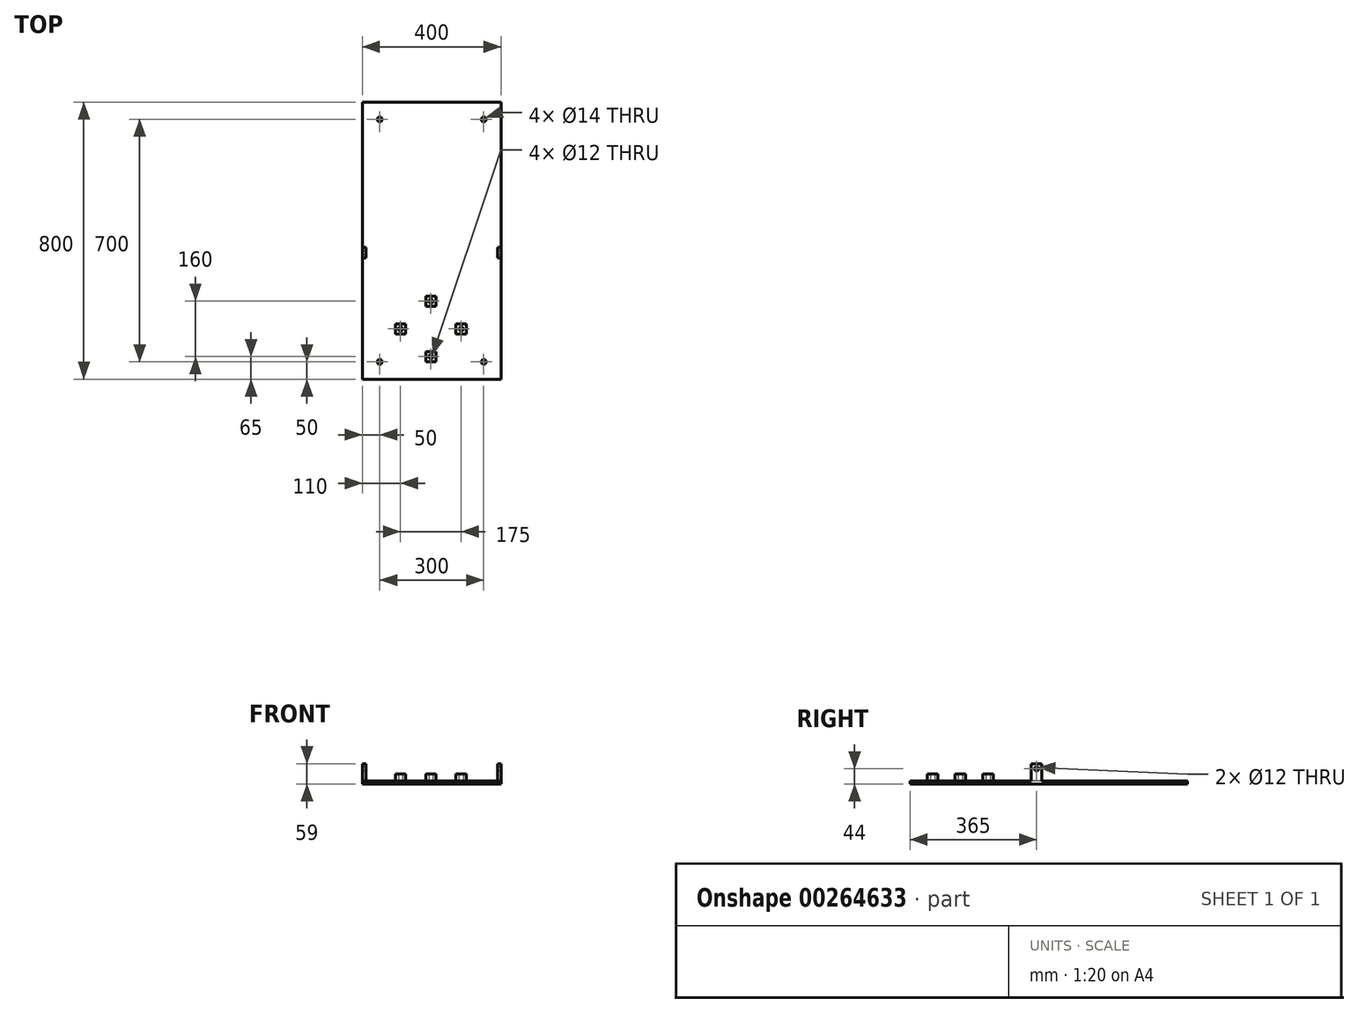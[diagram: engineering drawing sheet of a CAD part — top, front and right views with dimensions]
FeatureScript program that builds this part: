
annotation { "Feature Type Name" : "Feature", "Feature Type Description" : "" }
export const myFeature = defineFeature(function(context is Context, id is Id, definition is map)
    precondition{}
    {
        {
            var Q0;
            Q0=qCreatedBy(makeId("Top.planeOp"),FACE);
            var sketch = newSketch(context, id + "F0", { "sketchPlane" : qUnion([Q0])});
            skLineSegment(sketch, "E0.bottom", {"start": v(0, 0) * mm, "end": v(400, 0) * mm});
            skLineSegment(sketch, "E0.top", {"start": v(0, 800) * mm, "end": v(400, 800) * mm});
            skLineSegment(sketch, "E0.left", {"start": v(0, 0) * mm, "end": v(0, 800) * mm});
            skLineSegment(sketch, "E0.right", {"start": v(400, 0) * mm, "end": v(400, 800) * mm});
            skLineSegment(sketch, "E1.0", {"start": v(50, 50) * mm, "end": v(50, 750) * mm, "construction": true});
            skLineSegment(sketch, "E1.1", {"start": v(50, 50) * mm, "end": v(350, 50) * mm, "construction": true});
            skLineSegment(sketch, "E1.2", {"start": v(350, 50) * mm, "end": v(350, 750) * mm, "construction": true});
            skLineSegment(sketch, "E1.3", {"start": v(50, 750) * mm, "end": v(350, 750) * mm, "construction": true});
            skCircle(sketch, "E2", {"center": v(50, 50) * mm, "radius": 7 * mm});
            skCircle(sketch, "E3", {"center": v(50, 750) * mm, "radius": 7 * mm});
            skCircle(sketch, "E4", {"center": v(350, 750) * mm, "radius": 7 * mm});
            skCircle(sketch, "E5", {"center": v(350, 50) * mm, "radius": 7 * mm});
            skLineSegment(sketch, "E6.bottom", {"start": v(95, 160) * mm, "end": v(125, 160) * mm});
            skLineSegment(sketch, "E6.top", {"start": v(95, 130) * mm, "end": v(125, 130) * mm});
            skLineSegment(sketch, "E6.left", {"start": v(95, 160) * mm, "end": v(95, 130) * mm});
            skLineSegment(sketch, "E6.right", {"start": v(125, 160) * mm, "end": v(125, 130) * mm});
            skLineSegment(sketch, "E7.bottom", {"start": v(182.5, 240) * mm, "end": v(212.5, 240) * mm});
            skLineSegment(sketch, "E7.top", {"start": v(182.5, 210) * mm, "end": v(212.5, 210) * mm});
            skLineSegment(sketch, "E7.left", {"start": v(182.5, 240) * mm, "end": v(182.5, 210) * mm});
            skLineSegment(sketch, "E7.right", {"start": v(212.5, 240) * mm, "end": v(212.5, 210) * mm});
            skLineSegment(sketch, "E8.bottom", {"start": v(270, 160) * mm, "end": v(300, 160) * mm});
            skLineSegment(sketch, "E8.top", {"start": v(270, 130) * mm, "end": v(300, 130) * mm});
            skLineSegment(sketch, "E8.left", {"start": v(270, 160) * mm, "end": v(270, 130) * mm});
            skLineSegment(sketch, "E8.right", {"start": v(300, 160) * mm, "end": v(300, 130) * mm});
            skLineSegment(sketch, "E9.bottom", {"start": v(182.5, 80) * mm, "end": v(212.5, 80) * mm});
            skLineSegment(sketch, "E9.top", {"start": v(182.5, 50) * mm, "end": v(212.5, 50) * mm});
            skLineSegment(sketch, "E9.left", {"start": v(182.5, 80) * mm, "end": v(182.5, 50) * mm});
            skLineSegment(sketch, "E9.right", {"start": v(212.5, 80) * mm, "end": v(212.5, 50) * mm});
            skLineSegment(sketch, "E10", {"start": v(182.5, 50) * mm, "end": v(212.5, 80) * mm, "construction": true});
            skLineSegment(sketch, "E11", {"start": v(95, 130) * mm, "end": v(125, 160) * mm, "construction": true});
            skLineSegment(sketch, "E12", {"start": v(182.5, 210) * mm, "end": v(212.5, 240) * mm, "construction": true});
            skLineSegment(sketch, "E13", {"start": v(270, 130) * mm, "end": v(300, 160) * mm, "construction": true});
            skCircle(sketch, "E14", {"center": v(197.5, 65) * mm, "radius": 6 * mm});
            skCircle(sketch, "E15", {"center": v(110, 145) * mm, "radius": 6 * mm});
            skCircle(sketch, "E16", {"center": v(197.5, 225) * mm, "radius": 6 * mm});
            skCircle(sketch, "E17", {"center": v(285, 145) * mm, "radius": 6 * mm});
            skLineSegment(sketch, "E18", {"start": v(110, 145) * mm, "end": v(197.5, 145) * mm, "construction": true});
            skLineSegment(sketch, "E19", {"start": v(197.5, 145) * mm, "end": v(197.5, 225) * mm, "construction": true});
            skLineSegment(sketch, "E20", {"start": v(197.5, 145) * mm, "end": v(285, 145) * mm, "construction": true});
            skLineSegment(sketch, "E21", {"start": v(197.5, 145) * mm, "end": v(197.5, 65) * mm, "construction": true});
            skLineSegment(sketch, "E22", {"start": v(400, 380) * mm, "end": v(390, 380) * mm});
            skLineSegment(sketch, "E23", {"start": v(390, 380) * mm, "end": v(390, 350) * mm});
            skLineSegment(sketch, "E24", {"start": v(390, 350) * mm, "end": v(400, 350) * mm});
            skLineSegment(sketch, "E25", {"start": v(0, 380) * mm, "end": v(10, 380) * mm});
            skLineSegment(sketch, "E26", {"start": v(10, 380) * mm, "end": v(10, 350) * mm});
            skLineSegment(sketch, "E27", {"start": v(10, 350) * mm, "end": v(0, 350) * mm});
            skSolve(sketch);
        }
        {
            var Q0;
            Q0=makeQuery(id+"F0.imprint","IMPRINT",FACE,{"disambiguationData":[TD([[makeQuery(id+"F0.imprint","IMPRINT",EDGE,{"derivedFrom":sQuery(id+"F0.wireOp",EDGE,"E0.bottom")}),1.0]])]});
            extrude(context, id + "F1", {"entities" : qUnion([Q0]), "depth" : 9 * mm});
        }
        {
            var Q0;
            Q0=makeQuery(id+"F0.imprint","IMPRINT",FACE,{"disambiguationData":[TD([[makeQuery(id+"F0.imprint","IMPRINT",EDGE,{"derivedFrom":sQuery(id+"F0.wireOp",EDGE,"E6.bottom")}),-1.0]])]});
            var Q1;
            Q1=makeQuery(id+"F0.imprint","IMPRINT",FACE,{"disambiguationData":[TD([[makeQuery(id+"F0.imprint","IMPRINT",EDGE,{"derivedFrom":sQuery(id+"F0.wireOp",EDGE,"E7.bottom")}),-1.0]])]});
            var Q2;
            Q2=makeQuery(id+"F0.imprint","IMPRINT",FACE,{"disambiguationData":[TD([[makeQuery(id+"F0.imprint","IMPRINT",EDGE,{"derivedFrom":sQuery(id+"F0.wireOp",EDGE,"E9.bottom")}),-1.0]])]});
            var Q3;
            Q3=makeQuery(id+"F0.imprint","IMPRINT",FACE,{"disambiguationData":[TD([[makeQuery(id+"F0.imprint","IMPRINT",EDGE,{"derivedFrom":sQuery(id+"F0.wireOp",EDGE,"E8.bottom")}),-1.0]])]});
            extrude(context, id + "F2", {"entities" : qUnion([Q0, Q1, Q2, Q3]), "operationType" : NewBodyOperationType.ADD, "depth" : 29 * mm});
        }
        {
            var Q0;
            {var subQ0=sQuery(id+"F0.wireOp",EDGE,"E25");Q0=makeQuery(id+"F0.imprint","IMPRINT",FACE,{"disambiguationData":[TD([[makeQuery(id+"F0.imprint","IMPRINT",EDGE,{"derivedFrom":subQ0}),-1.0]])]});}
            var Q1;
            {var subQ0=sQuery(id+"F0.wireOp",EDGE,"E22");Q1=makeQuery(id+"F0.imprint","IMPRINT",FACE,{"disambiguationData":[TD([[makeQuery(id+"F0.imprint","IMPRINT",EDGE,{"derivedFrom":subQ0}),1.0]])]});}
            extrude(context, id + "F3", {"entities" : qUnion([Q0, Q1]), "operationType" : NewBodyOperationType.ADD, "depth" : 59 * mm});
        }
        {
            var Q0;
            Q0=qCreatedBy(makeId("Right.planeOp"),FACE);
            var sketch = newSketch(context, id + "F4", { "sketchPlane" : qUnion([Q0])});
            skLineSegment(sketch, "E28.0.0", {"start": v(350, 9) * mm, "end": v(380, 9) * mm, "construction": true});
            skLineSegment(sketch, "E28.0.1", {"start": v(380, 9) * mm, "end": v(380, 59) * mm, "construction": true});
            skLineSegment(sketch, "E28.0.2", {"start": v(380, 59) * mm, "end": v(350, 59) * mm, "construction": true});
            skLineSegment(sketch, "E28.0.3", {"start": v(350, 59) * mm, "end": v(350, 9) * mm, "construction": true});
            skLineSegment(sketch, "E29", {"start": v(365, 59) * mm, "end": v(365, 44) * mm, "construction": true});
            skLineSegment(sketch, "E30", {"start": v(365, 44) * mm, "end": v(350, 44) * mm, "construction": true});
            skLineSegment(sketch, "E31", {"start": v(365, 44) * mm, "end": v(380, 44) * mm, "construction": true});
            skCircle(sketch, "E32", {"center": v(365, 44) * mm, "radius": 6 * mm});
            skSolve(sketch);
        }
        {
            var Q0;
            Q0 = qSketchRegion(id + "F4", true);
            var Q1;
            Q1 = qConstructionFilter(qBodyType(qCreatedBy(id + "F4" ,EDGE), BodyType.WIRE), ConstructionObject.NO);
            extrude(context, id + "F5", {"entities" : qUnion([Q0]), "operationType" : NewBodyOperationType.REMOVE, "surfaceEntities" : qUnion([Q1]), "depth" : 486 * mm});
        }
    });
